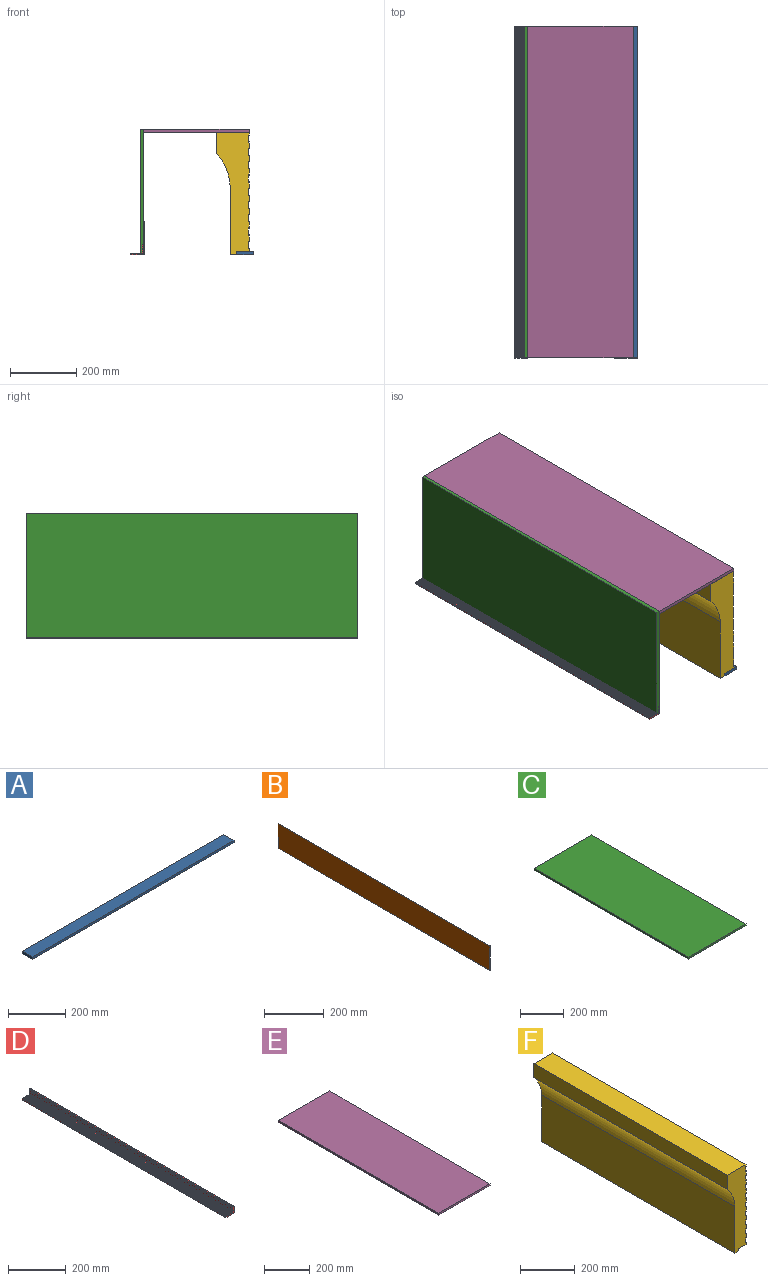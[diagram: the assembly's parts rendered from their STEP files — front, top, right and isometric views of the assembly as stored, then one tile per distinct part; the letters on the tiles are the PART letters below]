
ASSEMBLY  parts=6 mates=4
PART A: 6 faces, bbox 1000x50x10 mm
  f0: plane 1000x10mm, normal (0,-1,0), area 10000mm2, adj f1,f3,f4,f5
  f1: plane 1000x50mm, normal (0,0,-1), area 50000mm2, adj f0,f2,f4,f5
  f2: plane 1000x10mm, normal (0,1,0), area 10000mm2, adj f1,f3,f4,f5
  f3: plane 1000x50mm, normal (0,0,1), area 50000mm2, adj f0,f2,f4,f5
  f4: plane 50x10mm, normal (1,0,0), area 500mm2, adj f0,f1,f2,f3
  f5: plane 50x10mm, normal (-1,0,0), area 500mm2, adj f0,f1,f2,f3
PART B: 6 faces, bbox 1.5x1000x100 mm
  f0: plane 1000x100mm, normal (-1,0,0), area 100000mm2, adj f1,f3,f4,f5
  f1: plane 1000x1.5mm, normal (0,0,-1), area 1500mm2, adj f0,f2,f4,f5
  f2: plane 1000x100mm, normal (1,0,0), area 100000mm2, adj f1,f3,f4,f5
  f3: plane 1000x1.5mm, normal (0,0,1), area 1500mm2, adj f0,f2,f4,f5
  f4: plane 100x1.5mm, normal (0,-1,0), area 150mm2, adj f0,f1,f2,f3
  f5: plane 100x1.5mm, normal (0,1,0), area 150mm2, adj f0,f1,f2,f3
PART C: 6 faces, bbox 375x1000x10 mm
  f0: plane 1000x10mm, normal (-1,0,0), area 10000mm2, adj f1,f3,f4,f5
  f1: plane 1000x375mm, normal (0,0,-1), area 375000mm2, adj f0,f2,f4,f5
  f2: plane 1000x10mm, normal (1,0,0), area 10000mm2, adj f1,f3,f4,f5
  f3: plane 1000x375mm, normal (0,0,1), area 375000mm2, adj f0,f2,f4,f5
  f4: plane 375x10mm, normal (0,-1,0), area 3750mm2, adj f0,f1,f2,f3
  f5: plane 375x10mm, normal (0,1,0), area 3750mm2, adj f0,f1,f2,f3
PART D: 87 faces, bbox 40x1000x30 mm
  f0: plane 1000x1.4mm, normal (0,0,1), area 1400mm2, adj f1,f84,f85,f86
  f1: cylinder r=0.3mm len=1000mm, axis (0,1,0), area 314.2mm2, adj f0,f2,f85,f86
  f2: cylinder r=0.3mm len=1000mm, axis (0,1,0), area 314.2mm2, adj f1,f3,f85,f86
  f3: plane 1000x3.06mm, normal (0,0,1), area 3060.8mm2, adj f2,f4,f85,f86
  f4: cylinder r=0.3mm len=1000mm, axis (0,1,0), area 314.2mm2, adj f3,f5,f85,f86
  f5: cylinder r=0.3mm len=1000mm, axis (0,1,0), area 314.2mm2, adj f4,f6,f85,f86
  f6: plane 1000x1.4mm, normal (0,0,1), area 1400mm2, adj f5,f7,f85,f86
  f7: cylinder r=0.3mm len=1000mm, axis (0,1,0), area 314.2mm2, adj f6,f8,f85,f86
  f8: cylinder r=0.3mm len=1000mm, axis (0,1,0), area 314.2mm2, adj f7,f9,f85,f86
  f9: plane 1000x3.06mm, normal (0,0,1), area 3060.8mm2, adj f8,f10,f85,f86
  f10: cylinder r=0.3mm len=1000mm, axis (0,1,0), area 314.2mm2, adj f9,f11,f85,f86
  f11: cylinder r=0.3mm len=1000mm, axis (0,1,0), area 314.2mm2, adj f10,f12,f85,f86
  f12: plane 1000x1.4mm, normal (0,0,1), area 1400mm2, adj f11,f13,f85,f86
  f13: cylinder r=0.3mm len=1000mm, axis (0,1,0), area 314.2mm2, adj f12,f14,f85,f86
  f14: cylinder r=0.3mm len=1000mm, axis (0,1,0), area 314.2mm2, adj f13,f15,f85,f86
  f15: plane 1000x3.06mm, normal (0,0,1), area 3060.8mm2, adj f14,f16,f85,f86
  f16: cylinder r=0.3mm len=1000mm, axis (0,1,0), area 314.2mm2, adj f15,f17,f85,f86
  f17: cylinder r=0.3mm len=1000mm, axis (0,1,0), area 314.2mm2, adj f16,f18,f85,f86
  f18: plane 1000x1.4mm, normal (0,0,1), area 1400mm2, adj f17,f19,f85,f86
  f19: cylinder r=0.3mm len=1000mm, axis (0,1,0), area 314.2mm2, adj f18,f20,f85,f86
  f20: cylinder r=0.3mm len=1000mm, axis (0,1,0), area 314.2mm2, adj f19,f21,f85,f86
  f21: plane 1000x3.06mm, normal (0,0,1), area 3060.8mm2, adj f20,f22,f85,f86
  f22: cylinder r=0.3mm len=1000mm, axis (0,1,0), area 314.2mm2, adj f21,f23,f85,f86
  f23: cylinder r=0.3mm len=1000mm, axis (0,1,0), area 314.2mm2, adj f22,f24,f85,f86
  f24: plane 1000x1.4mm, normal (0,0,1), area 1400mm2, adj f23,f25,f85,f86
  f25: cylinder r=0.3mm len=1000mm, axis (0,1,0), area 314.2mm2, adj f24,f26,f85,f86
  f26: cylinder r=0.3mm len=1000mm, axis (0,1,0), area 314.2mm2, adj f25,f27,f85,f86
  f27: plane 1000x3.06mm, normal (0,0,1), area 3060.8mm2, adj f26,f28,f85,f86
  f28: cylinder r=0.3mm len=1000mm, axis (0,1,0), area 314.2mm2, adj f27,f29,f85,f86
  f29: cylinder r=0.3mm len=1000mm, axis (0,1,0), area 314.2mm2, adj f28,f30,f85,f86
  f30: plane 1000x1.4mm, normal (0,0,1), area 1400mm2, adj f29,f31,f85,f86
  f31: cylinder r=0.3mm len=1000mm, axis (0,1,0), area 314.2mm2, adj f30,f32,f85,f86
  f32: cylinder r=0.3mm len=1000mm, axis (0,1,0), area 314.2mm2, adj f31,f33,f85,f86
  f33: plane 1000x0.98mm, normal (0,0,1), area 980.4mm2, adj f32,f34,f85,f86
  f34: cylinder r=0.3mm len=1000mm, axis (0,1,0), area 471.2mm2, adj f33,f35,f85,f86
  f35: plane 1000x4.4mm, normal (-1,0,0), area 4400mm2, adj f34,f36,f85,f86
  f36: cylinder r=0.3mm len=1000mm, axis (0,1,0), area 471.2mm2, adj f35,f37,f85,f86
  f37: plane 1000x11.1mm, normal (0,0,-1), area 11095.9mm2, adj f36,f38,f85,f86
  f38: cylinder r=0.5mm len=1000mm, axis (0,1,0), area 397.7mm2, adj f37,f39,f85,f86
  f39: cylinder r=0.5mm len=1000mm, axis (0,1,0), area 795.4mm2, adj f38,f40,f85,f86
  f40: cylinder r=0.5mm len=1000mm, axis (0,1,0), area 397.7mm2, adj f39,f41,f85,f86
  f41: plane 1000x1.37mm, normal (0,0,-1), area 1371.7mm2, adj f40,f42,f85,f86
  f42: cylinder r=0.5mm len=1000mm, axis (0,1,0), area 397.7mm2, adj f41,f43,f85,f86
  f43: cylinder r=0.5mm len=1000mm, axis (0,1,0), area 795.4mm2, adj f42,f44,f85,f86
  f44: cylinder r=0.5mm len=1000mm, axis (0,1,0), area 397.7mm2, adj f43,f45,f85,f86
  f45: plane 1000x11.78mm, normal (0,0,-1), area 11775.9mm2, adj f44,f46,f85,f86
  f46: cylinder r=0.3mm len=1000mm, axis (0,1,0), area 471.2mm2, adj f45,f47,f85,f86
  f47: plane 1000x1.1mm, normal (1,0,0), area 1100mm2, adj f46,f48,f85,f86
  f48: plane 1000x1.4mm, normal (0,0,-1), area 1400mm2, adj f47,f49,f85,f86
  f49: plane 1000x1.1mm, normal (-1,0,0), area 1100mm2, adj f48,f50,f85,f86
  f50: cylinder r=0.3mm len=1000mm, axis (0,1,0), area 471.2mm2, adj f49,f51,f85,f86
  f51: plane 1000x10.3mm, normal (0,0,-1), area 10300mm2, adj f50,f52,f85,f86
  f52: cylinder r=0.3mm len=1000mm, axis (0,1,0), area 471.2mm2, adj f51,f53,f85,f86
  f53: plane 1000x10.3mm, normal (1,0,0), area 10300mm2, adj f52,f54,f85,f86
  f54: cylinder r=0.3mm len=1000mm, axis (0,1,0), area 471.2mm2, adj f53,f55,f85,f86
  f55: plane 1000x1.1mm, normal (0,0,1), area 1100mm2, adj f54,f56,f85,f86
  f56: plane 1000x1.4mm, normal (1,0,0), area 1400mm2, adj f55,f57,f85,f86
  f57: plane 1000x1.1mm, normal (0,0,-1), area 1100mm2, adj f56,f58,f85,f86
  f58: cylinder r=0.3mm len=1000mm, axis (0,1,0), area 471.2mm2, adj f57,f59,f85,f86
  f59: plane 1000x17.1mm, normal (1,0,0), area 17100mm2, adj f58,f60,f85,f86
  f60: cylinder r=0.3mm len=1000mm, axis (0,1,0), area 471.2mm2, adj f59,f61,f85,f86
  f61: plane 1000x4.4mm, normal (0,0,1), area 4400mm2, adj f60,f62,f85,f86
  f62: cylinder r=0.3mm len=1000mm, axis (0,1,0), area 471.2mm2, adj f61,f63,f85,f86
  f63: plane 1000x3.48mm, normal (-1,0,0), area 3480.4mm2, adj f62,f64,f85,f86
  f64: cylinder r=0.3mm len=1000mm, axis (0,1,0), area 314.2mm2, adj f63,f65,f85,f86
  f65: cylinder r=0.3mm len=1000mm, axis (0,1,0), area 314.2mm2, adj f64,f66,f85,f86
  f66: plane 1000x1.4mm, normal (-1,0,0), area 1400mm2, adj f65,f67,f85,f86
  f67: cylinder r=0.3mm len=1000mm, axis (0,1,0), area 314.2mm2, adj f66,f68,f85,f86
  f68: cylinder r=0.3mm len=1000mm, axis (0,1,0), area 314.2mm2, adj f67,f69,f85,f86
  f69: plane 1000x5.06mm, normal (-1,0,0), area 5060.8mm2, adj f68,f70,f85,f86
  f70: cylinder r=0.3mm len=1000mm, axis (0,1,0), area 314.2mm2, adj f69,f71,f85,f86
  f71: cylinder r=0.3mm len=1000mm, axis (0,1,0), area 314.2mm2, adj f70,f72,f85,f86
  f72: plane 1000x1.4mm, normal (-1,0,0), area 1400mm2, adj f71,f73,f85,f86
  f73: cylinder r=0.3mm len=1000mm, axis (0,1,0), area 314.2mm2, adj f72,f74,f85,f86
  f74: cylinder r=0.3mm len=1000mm, axis (0,1,0), area 314.2mm2, adj f73,f75,f85,f86
  f75: plane 1000x5.06mm, normal (-1,0,0), area 5060.8mm2, adj f74,f76,f85,f86
  f76: cylinder r=0.3mm len=1000mm, axis (0,1,0), area 314.2mm2, adj f75,f77,f85,f86
  f77: cylinder r=0.3mm len=1000mm, axis (0,1,0), area 314.2mm2, adj f76,f78,f85,f86
  f78: plane 1000x1.4mm, normal (-1,0,0), area 1400mm2, adj f77,f79,f85,f86
  f79: cylinder r=0.3mm len=1000mm, axis (0,1,0), area 314.2mm2, adj f78,f80,f85,f86
  f80: cylinder r=0.3mm len=1000mm, axis (0,1,0), area 314.2mm2, adj f79,f81,f85,f86
  f81: plane 1000x3.78mm, normal (-1,0,0), area 3780.4mm2, adj f80,f82,f85,f86
  f82: plane 1000x3.78mm, normal (0,0,1), area 3780.4mm2, adj f81,f83,f85,f86
  f83: cylinder r=0.3mm len=1000mm, axis (0,1,0), area 314.2mm2, adj f82,f84,f85,f86
  f84: cylinder r=0.3mm len=1000mm, axis (0,1,0), area 314.2mm2, adj f0,f83,f85,f86
  f85: plane 40x30mm, normal (0,-1,0), area 325.7mm2, adj f0,f1,f2,f3,f4,f5,f6,f7
  f86: plane 40x30mm, normal (0,1,0), area 325.7mm2, adj f0,f1,f2,f3,f4,f5,f6,f7
PART E: 6 faces, bbox 317x1000x10 mm
  f0: plane 1000x10mm, normal (-1,0,0), area 10000mm2, adj f1,f3,f4,f5
  f1: plane 1000x317mm, normal (0,0,-1), area 317000mm2, adj f0,f2,f4,f5
  f2: plane 1000x10mm, normal (1,0,0), area 10000mm2, adj f1,f3,f4,f5
  f3: plane 1000x317mm, normal (0,0,1), area 317000mm2, adj f0,f2,f4,f5
  f4: plane 317x10mm, normal (0,-1,0), area 3170mm2, adj f0,f1,f2,f3
  f5: plane 317x10mm, normal (0,1,0), area 3170mm2, adj f0,f1,f2,f3
PART F: 46 faces, bbox 97.1x1000x368.5 mm
  f0: plane 1000x97.1mm, normal (0,0,1), area 97100mm2, adj f1,f43,f44,f45
  f1: plane 1000x63.5mm, normal (-1,0,0), area 63500mm2, adj f0,f2,f44,f45
  f2: cylinder r=157.8mm len=1000mm, axis (0,1,0), area 105640.8mm2, adj f1,f3,f44,f45
  f3: plane 1000x209.35mm, normal (-1,0,0), area 209347.8mm2, adj f2,f4,f44,f45
  f4: plane 1000x20.1mm, normal (0,0,-1), area 20100mm2, adj f3,f5,f44,f45
  f5: plane 1000x10mm, normal (1,0,0), area 10000mm2, adj f4,f6,f44,f45
  f6: plane 1000x37mm, normal (0,0,-1), area 37000mm2, adj f5,f7,f44,f45
  f7: plane 1000x10mm, normal (1,0,0), area 10000mm2, adj f6,f8,f44,f45
  f8: plane 1000x2mm, normal (-0.45,0,0.89), area 2236.1mm2, adj f7,f9,f44,f45
  f9: plane 1000x22mm, normal (1,0,0), area 22000mm2, adj f8,f10,f44,f45
  f10: plane 1000x2mm, normal (-0.45,0,-0.89), area 2236.1mm2, adj f9,f11,f44,f45
  f11: plane 1000x20mm, normal (1,0,0), area 20000mm2, adj f10,f12,f44,f45
  f12: plane 1000x2mm, normal (-0.45,0,0.89), area 2236.1mm2, adj f11,f13,f44,f45
  f13: plane 1000x22mm, normal (1,0,0), area 22000mm2, adj f12,f14,f44,f45
  f14: plane 1000x2mm, normal (-0.51,0,-0.86), area 2319.9mm2, adj f13,f15,f44,f45
  f15: plane 1000x20.18mm, normal (1,0,0), area 20175.7mm2, adj f14,f16,f44,f45
  f16: plane 1000x2mm, normal (-0.45,0,0.89), area 2236.1mm2, adj f15,f17,f44,f45
  f17: plane 1000x22mm, normal (1,0,0), area 22000mm2, adj f16,f18,f44,f45
  f18: plane 1000x2mm, normal (-0.45,0,-0.89), area 2236.1mm2, adj f17,f19,f44,f45
  f19: plane 1000x20mm, normal (1,0,0), area 20000mm2, adj f18,f20,f44,f45
  f20: plane 1000x2mm, normal (-0.45,0,0.89), area 2236.1mm2, adj f19,f21,f44,f45
  f21: plane 1000x22mm, normal (1,0,0), area 22000mm2, adj f20,f22,f44,f45
  f22: plane 1000x2mm, normal (-0.45,0,-0.89), area 2236.1mm2, adj f21,f23,f44,f45
  f23: plane 1000x20mm, normal (1,0,0), area 20000mm2, adj f22,f24,f44,f45
  f24: plane 1000x2mm, normal (-0.45,0,0.89), area 2236.1mm2, adj f23,f25,f44,f45
  f25: plane 1000x22mm, normal (1,0,0), area 22000mm2, adj f24,f26,f44,f45
  f26: plane 1000x2mm, normal (-0.45,0,-0.89), area 2236.1mm2, adj f25,f27,f44,f45
  f27: plane 1000x20mm, normal (1,0,0), area 20000mm2, adj f26,f28,f44,f45
  f28: plane 1000x2mm, normal (-0.45,0,0.89), area 2236.1mm2, adj f27,f29,f44,f45
  f29: plane 1000x22mm, normal (1,0,0), area 22000mm2, adj f28,f30,f44,f45
  f30: plane 1000x2mm, normal (-0.45,0,-0.89), area 2236.1mm2, adj f29,f31,f44,f45
  f31: plane 1000x20mm, normal (1,0,0), area 20000mm2, adj f30,f32,f44,f45
  f32: plane 1000x2mm, normal (-0.45,0,0.89), area 2236.1mm2, adj f31,f33,f44,f45
  f33: plane 1000x22mm, normal (1,0,0), area 22000mm2, adj f32,f34,f44,f45
  f34: plane 1000x2mm, normal (-0.45,0,-0.89), area 2236.1mm2, adj f33,f35,f44,f45
  f35: plane 1000x20mm, normal (1,0,0), area 20000mm2, adj f34,f36,f44,f45
  f36: plane 1000x2mm, normal (-0.45,0,0.89), area 2236.1mm2, adj f35,f37,f44,f45
  f37: plane 1000x22mm, normal (1,0,0), area 22000mm2, adj f36,f38,f44,f45
  f38: plane 1000x2mm, normal (-0.45,0,-0.89), area 2236.1mm2, adj f37,f39,f44,f45
  f39: plane 1000x20mm, normal (1,0,0), area 20000mm2, adj f38,f40,f44,f45
  f40: plane 1000x2mm, normal (-0.45,0,0.89), area 2236.1mm2, adj f39,f41,f44,f45
  f41: plane 1000x22mm, normal (1,0,0), area 22000mm2, adj f40,f42,f44,f45
  f42: plane 1000x2mm, normal (-0.45,0,-0.89), area 2236.1mm2, adj f41,f43,f44,f45
  f43: plane 1000x8.5mm, normal (1,0,0), area 8500mm2, adj f0,f42,f44,f45
  f44: plane 368.5x97.1mm, normal (0,-1,0), area 24137.8mm2, adj f0,f1,f2,f3,f4,f5,f6,f7
  f45: plane 368.5x97.1mm, normal (0,1,0), area 24137.8mm2, adj f0,f1,f2,f3,f4,f5,f6,f7
PLACE A rot(axis=(0,0,-1),90deg) t=(-592.21,245.34,-319.41)mm
PLACE B t=(-500.6,245.34,-319.11)mm
PLACE C rot(axis=(0,-1,0),90deg) t=(-500.7,245.34,-315.91)mm
PLACE D t=(-520.6,245.34,-304.41)mm
PLACE E t=(-500.7,245.34,49.09)mm
PLACE F t=(-369.75,245.34,-109.41)mm
MATE fastened F.f44 <-> E.f4  axis (0,-1,0) through (-183.7,-754.66,49.09)mm
MATE fastened A.f4 <-> F.f44  axis (0,-1,0) through (-220.7,-754.66,-309.41)mm
MATE fastened E.f4 <-> C.f4  axis (0,-1,0) through (-500.7,-754.66,59.09)mm
MATE fastened B.f4 <-> D.f85  axis (0,-1,0) through (-500.6,-754.66,-319.11)mm
